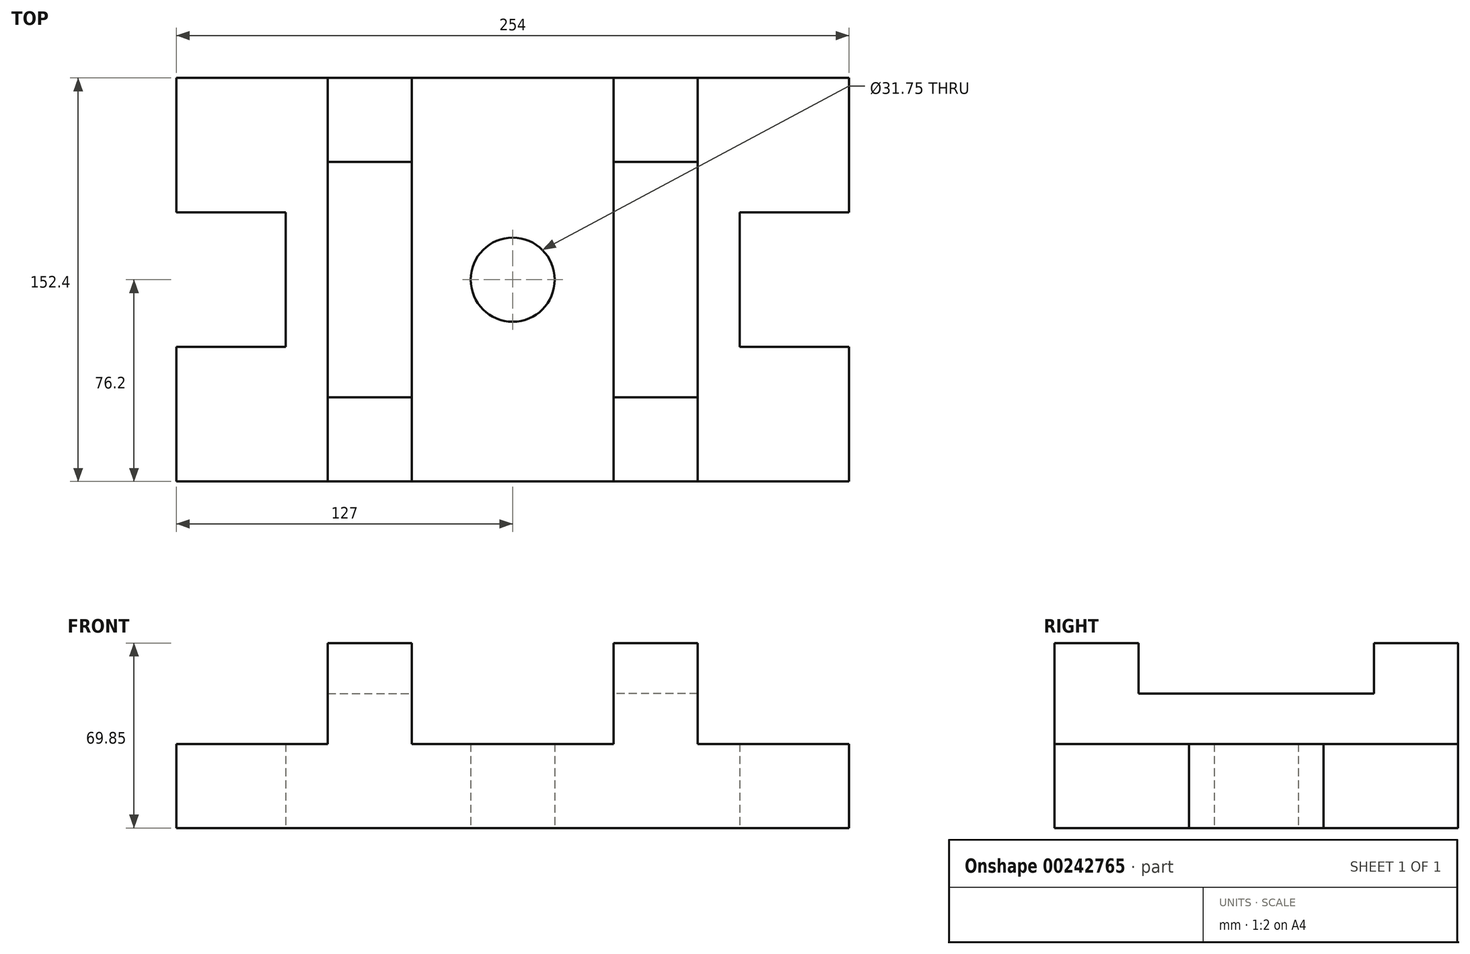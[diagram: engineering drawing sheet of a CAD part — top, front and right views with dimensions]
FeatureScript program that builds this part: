
annotation { "Feature Type Name" : "Feature", "Feature Type Description" : "" }
export const myFeature = defineFeature(function(context is Context, id is Id, definition is map)
    precondition{}
    {
        {
            var Q0;
            Q0=qCreatedBy(makeId("Top.planeOp"),FACE);
            var sketch = newSketch(context, id + "F0", { "sketchPlane" : qUnion([Q0])});
            skLineSegment(sketch, "E0.right", {"start": v(69.85, 76.2) * mm, "end": v(69.85, -76.2) * mm});
            skPoint(sketch, "E0.middle", {"position": v(0, 0) * mm});
            skLineSegment(sketch, "E1.top", {"start": v(-85.73, 25.4) * mm, "end": v(-127, 25.4) * mm});
            skLineSegment(sketch, "E1.right", {"start": v(-127, 76.2) * mm, "end": v(-127, 25.4) * mm});
            skLineSegment(sketch, "E2.right", {"start": v(-85.73, 25.4) * mm, "end": v(-85.73, -25.4) * mm});
            skLineSegment(sketch, "E3.top", {"start": v(-85.73, -25.4) * mm, "end": v(-127, -25.4) * mm});
            skLineSegment(sketch, "E3.right", {"start": v(-127, -76.2) * mm, "end": v(-127, -25.4) * mm});
            skLineSegment(sketch, "E4.bottom", {"start": v(-127, 76.2) * mm, "end": v(127, 76.2) * mm});
            skLineSegment(sketch, "E4.right", {"start": v(127, 76.2) * mm, "end": v(127, 25.4) * mm});
            skLineSegment(sketch, "E5.bottom", {"start": v(-127, -76.2) * mm, "end": v(127, -76.2) * mm});
            skLineSegment(sketch, "E5.top", {"start": v(85.73, -25.4) * mm, "end": v(127, -25.4) * mm});
            skLineSegment(sketch, "E5.right", {"start": v(127, -76.2) * mm, "end": v(127, -25.4) * mm});
            skLineSegment(sketch, "E6", {"start": v(127, 25.4) * mm, "end": v(85.72, 25.4) * mm});
            skLineSegment(sketch, "E7.right", {"start": v(85.73, 25.4) * mm, "end": v(85.73, -25.4) * mm});
            skLineSegment(sketch, "E8.right", {"start": v(-38.1, 76.2) * mm, "end": v(-38.1, -76.2) * mm});
            skLineSegment(sketch, "E9.right", {"start": v(38.1, 76.2) * mm, "end": v(38.1, -76.2) * mm});
            skLineSegment(sketch, "E10.top", {"start": v(-69.85, 44.45) * mm, "end": v(-38.1, 44.45) * mm});
            skLineSegment(sketch, "E11.top", {"start": v(69.85, 44.45) * mm, "end": v(38.1, 44.45) * mm});
            skLineSegment(sketch, "E12.top", {"start": v(-69.85, -44.45) * mm, "end": v(-38.1, -44.45) * mm});
            skLineSegment(sketch, "E13.top", {"start": v(69.85, -44.45) * mm, "end": v(38.1, -44.45) * mm});
            skCircle(sketch, "E14", {"center": v(0, 0) * mm, "radius": 15.88 * mm});
            skLineSegment(sketch, "E15", {"start": v(-69.85, -76.2) * mm, "end": v(-69.85, 76.2) * mm});
            skSolve(sketch);
        }
        {
            var Q0;
            Q0=makeQuery(id+"F0.imprint","IMPRINT",FACE,{"disambiguationData":[TD([[makeQuery(id+"F0.imprint","IMPRINT",EDGE,{"derivedFrom":sQuery(id+"F0.wireOp",EDGE,"E1.top")}),-1.0]])]});
            var Q1;
            Q1=makeQuery(id+"F0.imprint","IMPRINT",FACE,{"disambiguationData":[TD([[makeQuery(id+"F0.imprint","IMPRINT",EDGE,{"derivedFrom":sQuery(id+"F0.wireOp",EDGE,"E14")}),-1.0]])]});
            var Q2;
            {var subQ3=sQuery(id+"F0.wireOp",EDGE,"E4.right");Q2=makeQuery(id+"F0.imprint","IMPRINT",FACE,{"disambiguationData":[TD([[makeQuery(id+"F0.imprint","IMPRINT",EDGE,{"derivedFrom":subQ3}),-1.0]])]});}
            extrude(context, id + "F1", {"entities" : qUnion([Q0, Q1, Q2]), "depth" : 31.75 * mm});
        }
        {
            var Q0;
            {var subQ0=sQuery(id+"F0.wireOp",EDGE,"E10.top");Q0=makeQuery(id+"F0.imprint","IMPRINT",FACE,{"disambiguationData":[TD([[makeQuery(id+"F0.imprint","IMPRINT",EDGE,{"derivedFrom":subQ0}),-1.0]])]});}
            var Q1;
            {var subQ0=sQuery(id+"F0.wireOp",EDGE,"E11.top");Q1=makeQuery(id+"F0.imprint","IMPRINT",FACE,{"disambiguationData":[TD([[makeQuery(id+"F0.imprint","IMPRINT",EDGE,{"derivedFrom":subQ0}),1.0]])]});}
            extrude(context, id + "F2", {"entities" : qUnion([Q0, Q1]), "operationType" : NewBodyOperationType.ADD, "depth" : 50.8 * mm});
        }
        {
            var Q0;
            {var subQ0=sQuery(id+"F0.wireOp",EDGE,"E10.bottom");Q0=makeQuery(id+"F0.imprint","IMPRINT",FACE,{"disambiguationData":[TD([[makeQuery(id+"F0.imprint","IMPRINT",EDGE,{"derivedFrom":subQ0}),-1.0]])]});}
            var Q1;
            {var subQ0=sQuery(id+"F0.wireOp",EDGE,"E12.bottom");Q1=makeQuery(id+"F0.imprint","IMPRINT",FACE,{"disambiguationData":[TD([[makeQuery(id+"F0.imprint","IMPRINT",EDGE,{"derivedFrom":subQ0}),1.0]])]});}
            var Q2;
            {var subQ0=sQuery(id+"F0.wireOp",EDGE,"E11.bottom");Q2=makeQuery(id+"F0.imprint","IMPRINT",FACE,{"disambiguationData":[TD([[makeQuery(id+"F0.imprint","IMPRINT",EDGE,{"derivedFrom":subQ0}),1.0]])]});}
            var Q3;
            {var subQ2=sQuery(id+"F0.wireOp",EDGE,"E13.top");Q3=makeQuery(id+"F0.imprint","IMPRINT",FACE,{"disambiguationData":[TD([[makeQuery(id+"F0.imprint","IMPRINT",EDGE,{"derivedFrom":subQ2}),1.0]])]});}
            var Q4;
            {var subQ5=sQuery(id+"F0.wireOp",EDGE,"E10.top");Q4=makeQuery(id+"F0.imprint","IMPRINT",FACE,{"disambiguationData":[TD([[makeQuery(id+"F0.imprint","IMPRINT",EDGE,{"derivedFrom":subQ5}),1.0]])]});}
            var Q5;
            {var subQ5=sQuery(id+"F0.wireOp",EDGE,"E12.top");Q5=makeQuery(id+"F0.imprint","IMPRINT",FACE,{"disambiguationData":[TD([[makeQuery(id+"F0.imprint","IMPRINT",EDGE,{"derivedFrom":subQ5}),-1.0]])]});}
            var Q6;
            {var subQ3=sQuery(id+"F0.wireOp",EDGE,"E11.top");Q6=makeQuery(id+"F0.imprint","IMPRINT",FACE,{"disambiguationData":[TD([[makeQuery(id+"F0.imprint","IMPRINT",EDGE,{"derivedFrom":subQ3}),-1.0]])]});}
            extrude(context, id + "F3", {"entities" : qUnion([Q0, Q1, Q2, Q3, Q4, Q5, Q6]), "operationType" : NewBodyOperationType.ADD, "depth" : 69.85 * mm});
        }
    });
